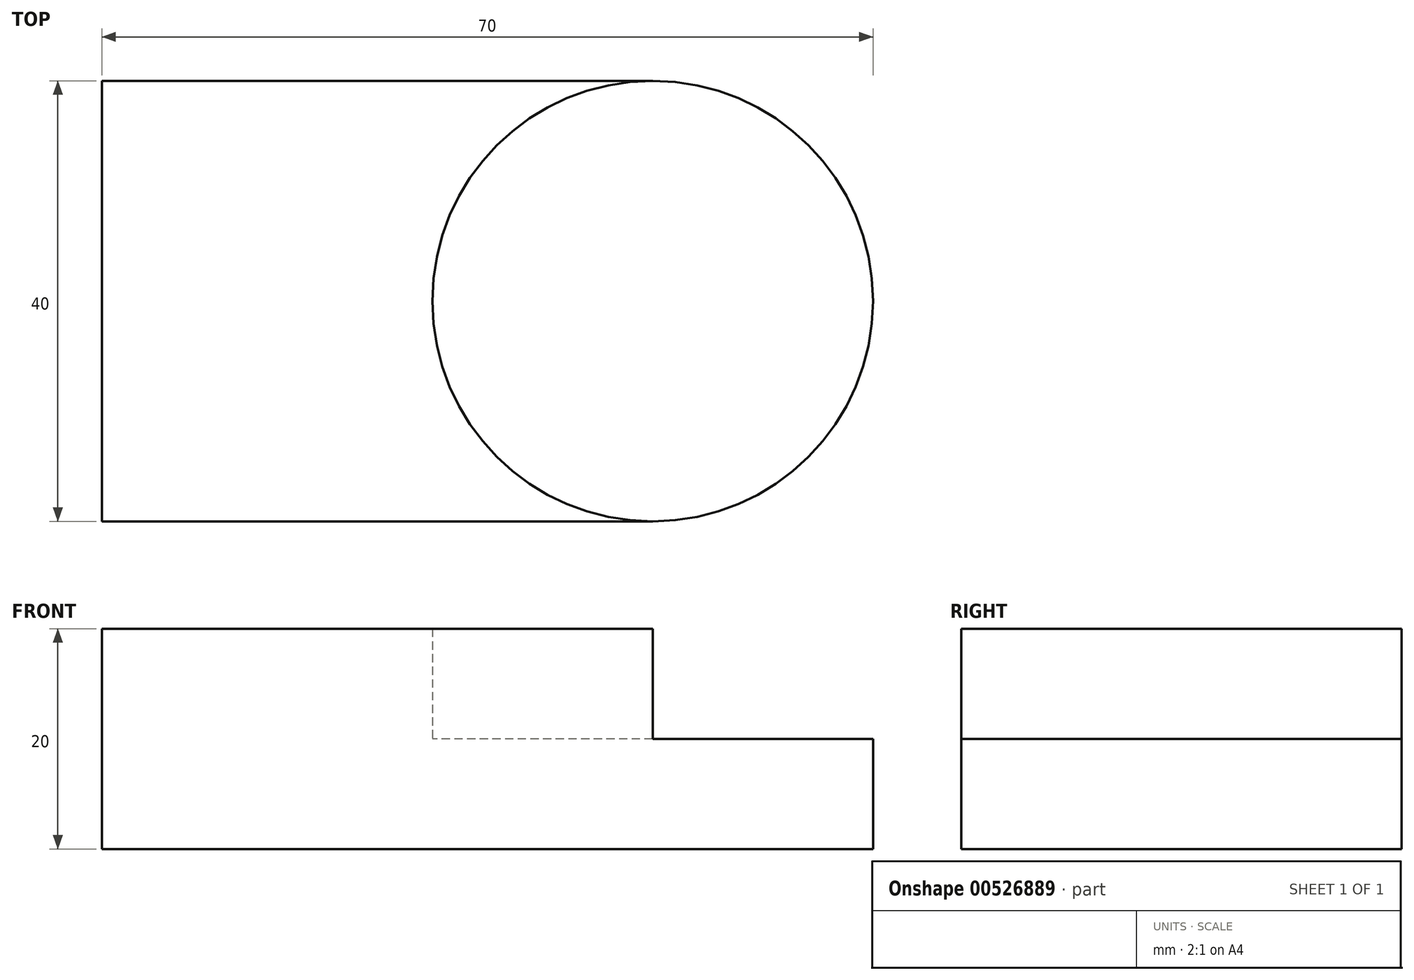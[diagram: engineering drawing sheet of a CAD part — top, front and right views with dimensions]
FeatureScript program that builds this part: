
annotation { "Feature Type Name" : "Feature", "Feature Type Description" : "" }
export const myFeature = defineFeature(function(context is Context, id is Id, definition is map)
    precondition{}
    {
        {
            var Q0;
            Q0=qCreatedBy(makeId("Top.planeOp"),FACE);
            var sketch = newSketch(context, id + "F0", { "sketchPlane" : qUnion([Q0])});
            skLineSegment(sketch, "E0.bottom", {"start": v(0, 0) * mm, "end": v(50, 0) * mm});
            skLineSegment(sketch, "E0.top", {"start": v(0, -40) * mm, "end": v(50, -40) * mm});
            skLineSegment(sketch, "E0.left", {"start": v(0, 0) * mm, "end": v(0, -40) * mm});
            skLineSegment(sketch, "E0.right", {"start": v(50, 0) * mm, "end": v(50, -40) * mm});
            skCircle(sketch, "E1", {"center": v(50, -20) * mm, "radius": 20 * mm});
            skSolve(sketch);
        }
        {
            var Q0;
            {var subQ0=sQuery(id+"F0.wireOp",EDGE,"E0.bottom");Q0=makeQuery(id+"F0.imprint","IMPRINT",FACE,{"disambiguationData":[TD([[makeQuery(id+"F0.imprint","IMPRINT",EDGE,{"derivedFrom":subQ0}),-1.0]])]});}
            extrude(context, id + "F1", {"entities" : qUnion([Q0]), "endBound" : BoundingType.SYMMETRIC, "depth" : 20 * mm, "offsetDistance" : 25 * mm});
        }
        {
            var Q0;
            {var subQ0=sQuery(id+"F0.wireOp",EDGE,"E0.right");Q0=makeQuery(id+"F0.imprint","IMPRINT",FACE,{"disambiguationData":[TD([[makeQuery(id+"F0.imprint","IMPRINT",EDGE,{"derivedFrom":subQ0}),-1.0]])]});}
            var Q1;
            {var subQ0=sQuery(id+"F0.wireOp",EDGE,"E0.right");Q1=makeQuery(id+"F0.imprint","IMPRINT",FACE,{"disambiguationData":[TD([[makeQuery(id+"F0.imprint","IMPRINT",EDGE,{"derivedFrom":subQ0}),1.0]])]});}
            extrude(context, id + "F2", {"entities" : qUnion([Q0, Q1]), "operationType" : NewBodyOperationType.ADD, "oppositeDirection" : true, "depth" : 10 * mm, "offsetDistance" : 25 * mm});
        }
    });
